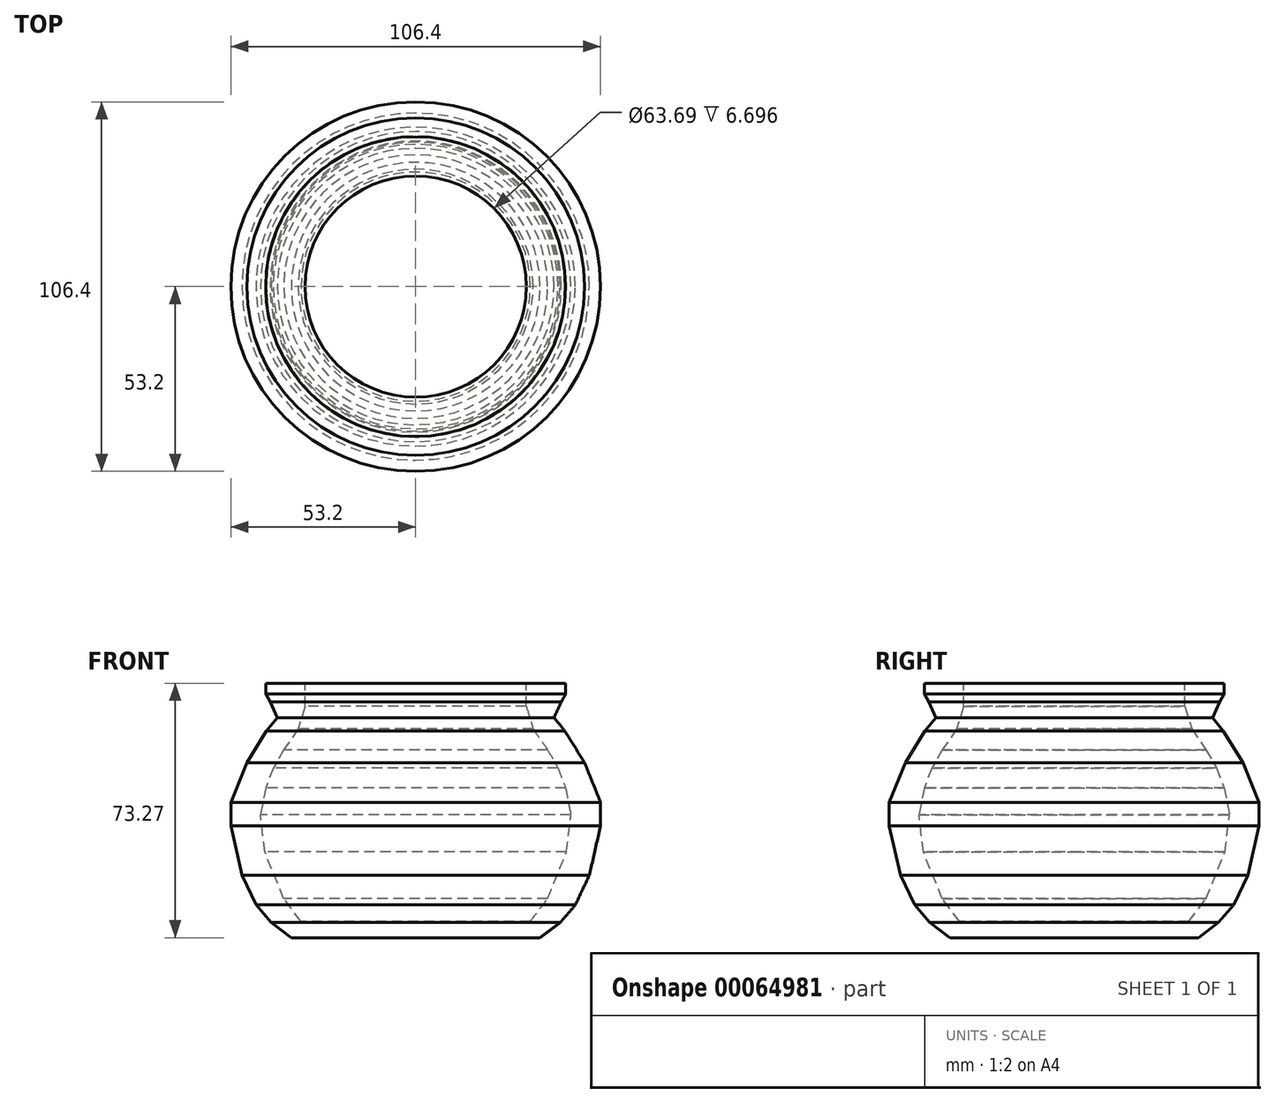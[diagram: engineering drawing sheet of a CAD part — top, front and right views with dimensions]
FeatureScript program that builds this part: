
annotation { "Feature Type Name" : "Feature", "Feature Type Description" : "" }
export const myFeature = defineFeature(function(context is Context, id is Id, definition is map)
    precondition{}
    {
        {
            var Q0;
            Q0=qCreatedBy(makeId("Front.planeOp"),FACE);
            var sketch = newSketch(context, id + "F0", { "sketchPlane" : qUnion([Q0])});
            skLineSegment(sketch, "E0", {"start": v(0, 0) * mm, "end": v(0, -63.38) * mm});
            skLineSegment(sketch, "E1", {"start": v(0, -63.38) * mm, "end": v(35.8, -63.38) * mm});
            skLineSegment(sketch, "E2", {"start": v(35.8, -63.38) * mm, "end": v(41.54, -59.03) * mm});
            skLineSegment(sketch, "E3", {"start": v(41.54, -59.03) * mm, "end": v(45.93, -53.95) * mm});
            skLineSegment(sketch, "E4", {"start": v(45.93, -53.95) * mm, "end": v(49.97, -45.41) * mm});
            skLineSegment(sketch, "E5", {"start": v(49.97, -45.41) * mm, "end": v(53.2, -31.2) * mm});
            skLineSegment(sketch, "E6", {"start": v(53.2, -31.2) * mm, "end": v(53.2, -24.4) * mm});
            skLineSegment(sketch, "E7", {"start": v(53.2, -24.4) * mm, "end": v(48.58, -12.97) * mm});
            skLineSegment(sketch, "E8", {"start": v(48.58, -12.97) * mm, "end": v(42.93, -3.85) * mm});
            skLineSegment(sketch, "E9", {"start": v(42.93, -3.85) * mm, "end": v(39.8, 0) * mm});
            skLineSegment(sketch, "E10", {"start": v(39.8, 0) * mm, "end": v(41.89, 4.47) * mm});
            skLineSegment(sketch, "E11", {"start": v(41.89, 4.47) * mm, "end": v(43.16, 6.78) * mm});
            skLineSegment(sketch, "E12", {"start": v(43.16, 6.78) * mm, "end": v(43.16, 9.9) * mm});
            skLineSegment(sketch, "E13", {"start": v(43.16, 9.9) * mm, "end": v(31.84, 9.9) * mm});
            skLineSegment(sketch, "E14", {"start": v(31.84, 9.9) * mm, "end": v(31.84, 3.2) * mm});
            skLineSegment(sketch, "E15", {"start": v(31.84, 3.2) * mm, "end": v(33.8, -3.27) * mm});
            skLineSegment(sketch, "E16", {"start": v(33.8, -3.27) * mm, "end": v(37.96, -9.27) * mm});
            skLineSegment(sketch, "E17", {"start": v(37.96, -9.27) * mm, "end": v(40.96, -14.58) * mm});
            skLineSegment(sketch, "E18", {"start": v(40.96, -14.58) * mm, "end": v(43.16, -20.24) * mm});
            skLineSegment(sketch, "E19", {"start": v(43.16, -20.24) * mm, "end": v(44.66, -27.98) * mm});
            skLineSegment(sketch, "E20", {"start": v(44.66, -27.98) * mm, "end": v(43.39, -38.71) * mm});
            skLineSegment(sketch, "E21", {"start": v(43.39, -38.71) * mm, "end": v(37.96, -52.1) * mm});
            skLineSegment(sketch, "E22", {"start": v(37.96, -52.1) * mm, "end": v(33, -58.69) * mm});
            skLineSegment(sketch, "E23", {"start": v(33, -58.69) * mm, "end": v(0, -58.69) * mm});
            skSolve(sketch);
        }
        {
            var Q0;
            Q0 = qSketchRegion(id + "F0", true);
            var Q1;
            Q1=sQuery(id+"F0.wireOp",EDGE,"E0");
            revolve(context, id + "F1", {"entities" : qUnion([Q0]), "axis" : qUnion([Q1]), "revolveType" : RevolveType.FULL});
        }
    });
